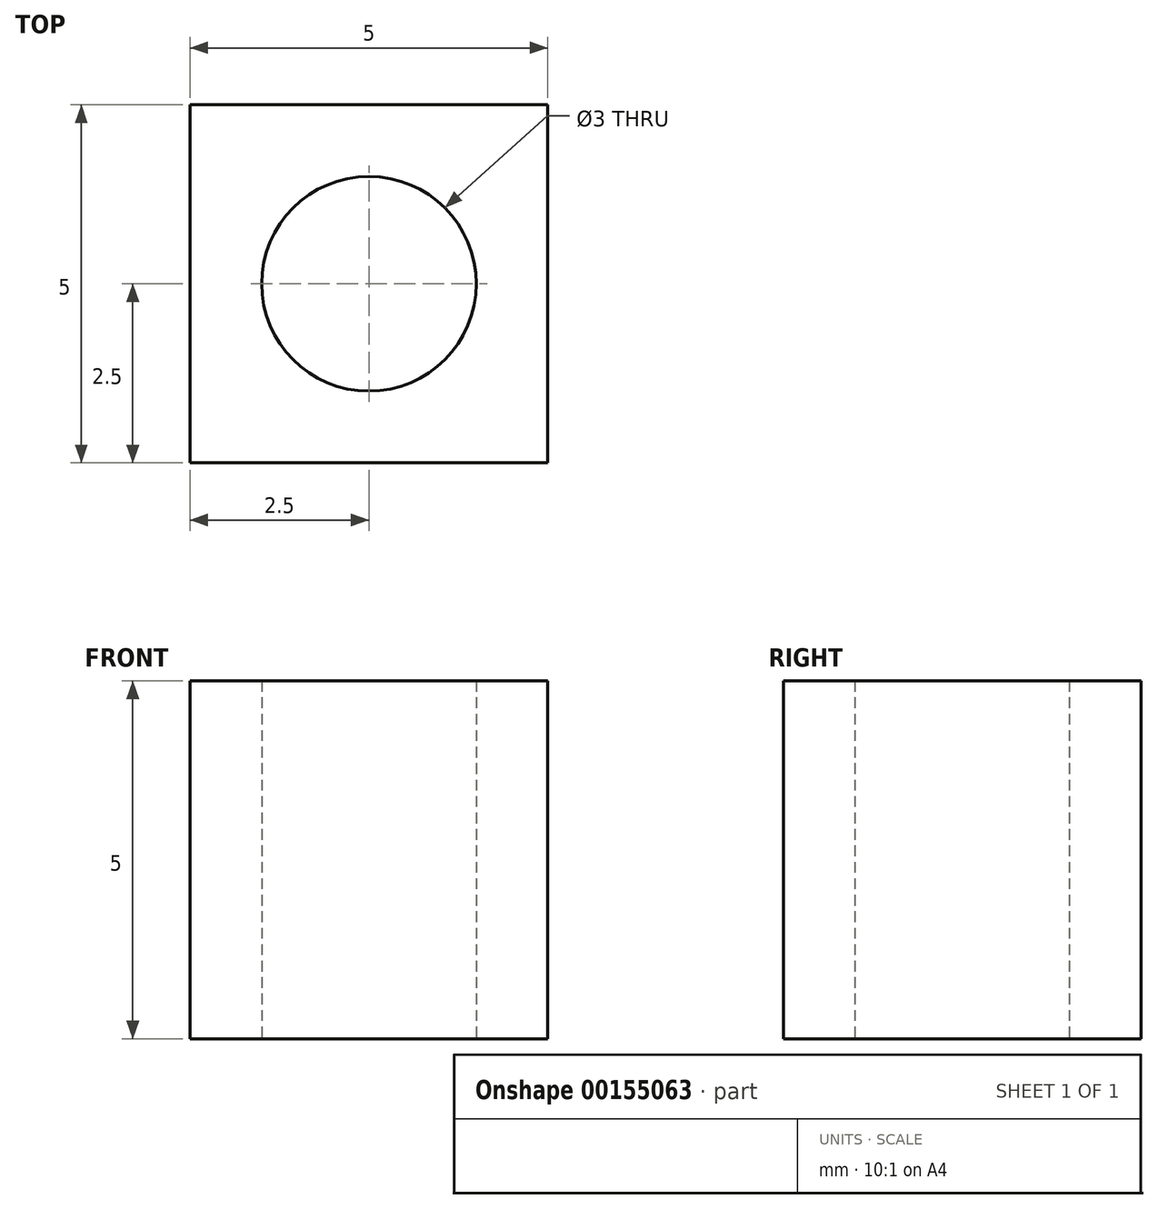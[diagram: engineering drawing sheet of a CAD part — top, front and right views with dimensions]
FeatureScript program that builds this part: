
annotation { "Feature Type Name" : "Feature", "Feature Type Description" : "" }
export const myFeature = defineFeature(function(context is Context, id is Id, definition is map)
    precondition{}
    {
        {
            var Q0;
            Q0=qCreatedBy(makeId("Top.planeOp"),FACE);
            var sketch = newSketch(context, id + "F0", { "sketchPlane" : qUnion([Q0])});
            skCircle(sketch, "E0", {"center": v(0, 0) * mm, "radius": 1.5 * mm});
            skLineSegment(sketch, "E1.bottom", {"start": v(-2.5, 2.5) * mm, "end": v(2.5, 2.5) * mm});
            skLineSegment(sketch, "E1.top", {"start": v(-2.5, -2.5) * mm, "end": v(2.5, -2.5) * mm});
            skLineSegment(sketch, "E1.left", {"start": v(-2.5, 2.5) * mm, "end": v(-2.5, -2.5) * mm});
            skLineSegment(sketch, "E1.right", {"start": v(2.5, 2.5) * mm, "end": v(2.5, -2.5) * mm});
            skLineSegment(sketch, "E2", {"start": v(-2.5, -2.5) * mm, "end": v(2.5, 2.5) * mm, "construction": true});
            skLineSegment(sketch, "E3", {"start": v(2.5, -2.5) * mm, "end": v(-2.5, 2.5) * mm, "construction": true});
            skSolve(sketch);
        }
        {
            var Q0;
            Q0=makeQuery(id+"F0.imprint","IMPRINT",FACE,{"disambiguationData":[TD([[makeQuery(id+"F0.imprint","IMPRINT",EDGE,{"derivedFrom":sQuery(id+"F0.wireOp",EDGE,"E0")}),-1.0]])]});
            extrude(context, id + "F1", {"entities" : qUnion([Q0]), "depth" : 5 * mm});
        }
    });
